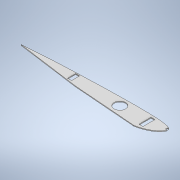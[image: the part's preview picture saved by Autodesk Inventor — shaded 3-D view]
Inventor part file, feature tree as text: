
AUTODESK INVENTOR PART (.ipt)
format: ipt  version: 2021 (Build 250183000, 183)  size: 151,040 bytes
history: native  units: mm
features: extrude x1, sketch x1
ambient origin geometry x8: Origin, YZ Plane, XZ Plane, XY Plane, X Axis, Y Axis, Z Axis, Center Point
bodies: Body1 (feature_tree)
feature tree (2):
  extrude  "Extrusion3"  Depth=2.0mm
  sketch  "Sketch1"  dims[d5=160.0mm d8=160.0mm d9=28.5mm d10=18.5mm d11=10.0mm d12=30.0mm d13=10.0mm d14=20.0mm d17=5.0mm d18=5.0mm d25=6.0mm d26=5.0mm d27=5.0mm d28=2.0mm d29=0.0mm]
